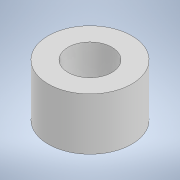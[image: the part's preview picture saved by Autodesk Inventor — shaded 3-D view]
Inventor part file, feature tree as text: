
AUTODESK INVENTOR PART (.ipt)
format: ipt  version: 2022.2 (Build 262287000, 287)  size: 94,720 bytes
history: native  units: mm
features: extrude x1, sketch x1
ambient origin geometry x8: Origin, YZ Plane, XZ Plane, XY Plane, X Axis, Y Axis, Z Axis, Center Point
bodies: Solid1 (feature_tree)
feature tree (2):
  extrude  "Extrusion1"  Depth=5.0mm
  sketch  "Sketch1"  dims[d0=4.2mm d1=8.0mm d2=5.0mm d3=0.0mm]
